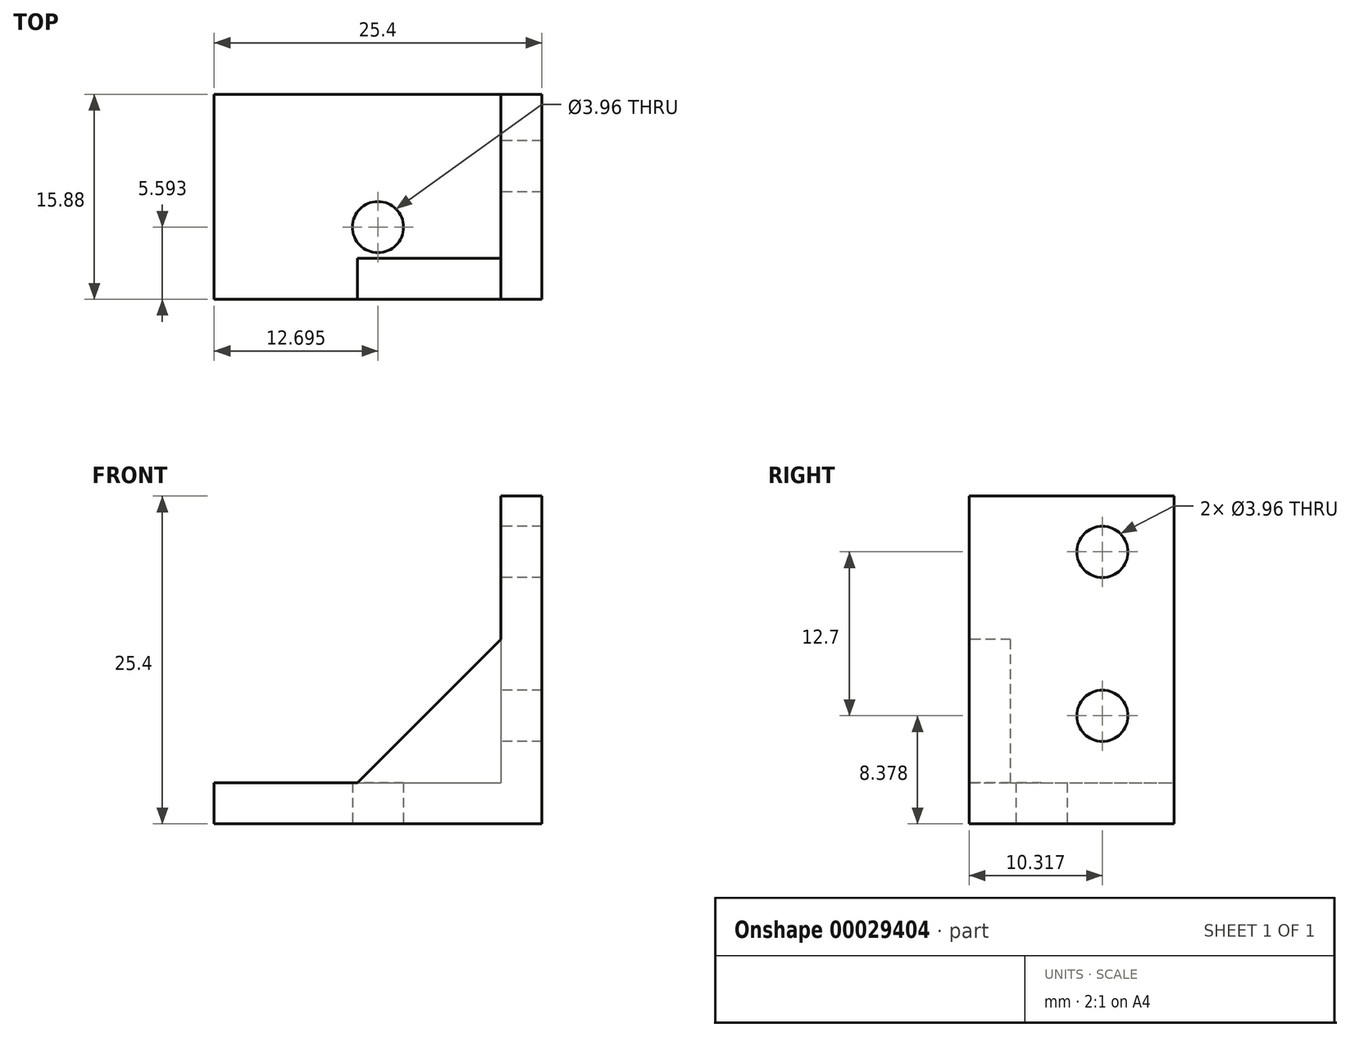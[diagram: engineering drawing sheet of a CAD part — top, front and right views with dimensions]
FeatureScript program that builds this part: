
annotation { "Feature Type Name" : "Feature", "Feature Type Description" : "" }
export const myFeature = defineFeature(function(context is Context, id is Id, definition is map)
    precondition{}
    {
        {
            var Q0;
            Q0=qCreatedBy(makeId("Front.planeOp"),FACE);
            var sketch = newSketch(context, id + "F0", { "sketchPlane" : qUnion([Q0])});
            skLineSegment(sketch, "E0.bottom", {"start": v(-17.16, -5.26) * mm, "end": v(5.06, -5.26) * mm});
            skLineSegment(sketch, "E0.top", {"start": v(-17.16, -8.43) * mm, "end": v(8.24, -8.43) * mm});
            skLineSegment(sketch, "E0.left", {"start": v(-17.16, -5.26) * mm, "end": v(-17.16, -8.43) * mm});
            skLineSegment(sketch, "E0.right", {"start": v(8.24, -5.26) * mm, "end": v(8.24, -8.43) * mm});
            skLineSegment(sketch, "E1", {"start": v(8.24, 16.97) * mm, "end": v(8.24, -8.43) * mm});
            skLineSegment(sketch, "E2", {"start": v(8.24, 16.97) * mm, "end": v(5.06, 16.97) * mm});
            skLineSegment(sketch, "E3", {"start": v(5.06, 16.97) * mm, "end": v(5.06, -5.26) * mm});
            skLineSegment(sketch, "E4", {"start": v(5.06, 5.85) * mm, "end": v(-6.05, -5.26) * mm});
            skLineSegment(sketch, "E5", {"start": v(-2.38, 7.14) * mm, "end": v(7.14, -2.38) * mm});
            skSolve(sketch);
        }
        {
            var Q0;
            {var subQ5=sQuery(id+"F0.wireOp",EDGE,"E0.top");Q0=makeQuery(id+"F0.imprint","IMPRINT",FACE,{"disambiguationData":[TD([[makeQuery(id+"F0.imprint","IMPRINT",EDGE,{"derivedFrom":subQ5}),1.0]])]});}
            extrude(context, id + "F1", {"entities" : qUnion([Q0]), "depth" : 15.88 * mm});
        }
        {
            var Q0;
            Q0=makeQuery(id+"F1.opExtrude","CAP_FACE",FACE,{"disambiguationData":[OSD([sQuery(id+"F0.wireOp",EDGE,"E0.bottom"),sQuery(id+"F0.wireOp",EDGE,"E0.top"),sQuery(id+"F0.wireOp",EDGE,"E0.left"),sQuery(id+"F0.wireOp",EDGE,"E1"),sQuery(id+"F0.wireOp",EDGE,"E2"),sQuery(id+"F0.wireOp",EDGE,"E3")])],"isStart":false});
            var sketch = newSketch(context, id + "F2", { "sketchPlane" : qUnion([Q0])});
            skLineSegment(sketch, "E6", {"start": v(5.06, 5.85) * mm, "end": v(-6.05, -5.26) * mm});
            skSolve(sketch);
        }
        {
            var Q0;
            {var subQ1=sQuery(id+"F2.wireOp",EDGE,"E6");Q0=makeQuery(id+"F2.imprint","IMPRINT",FACE,{"disambiguationData":[TD([[makeQuery(id+"F2.imprint","IMPRINT",EDGE,{"derivedFrom":subQ1}),1.0]])]});}
            extrude(context, id + "F3", {"entities" : qUnion([Q0]), "operationType" : NewBodyOperationType.ADD, "oppositeDirection" : true, "depth" : 3.17 * mm});
        }
        {
            var Q0;
            Q0=makeQuery(id+"F1.opExtrude","SWEPT_FACE",FACE,{"disambiguationData":[OSD([sQuery(id+"F0.wireOp",EDGE,"E3")])]});
            var sketch = newSketch(context, id + "F4", { "sketchPlane" : qUnion([Q0])});
            skCircle(sketch, "E7", {"center": v(5.56, 12.65) * mm, "radius": 1.98 * mm});
            skCircle(sketch, "E8", {"center": v(5.56, -0.05) * mm, "radius": 1.98 * mm});
            skSolve(sketch);
        }
        {
            var Q0;
            Q0=makeQuery(id+"F4.imprint","IMPRINT",FACE,{"disambiguationData":[TD([[makeQuery(id+"F4.imprint","IMPRINT",EDGE,{"derivedFrom":sQuery(id+"F4.wireOp",EDGE,"E7")}),1.0]])]});
            var Q1;
            Q1=makeQuery(id+"F4.imprint","IMPRINT",FACE,{"disambiguationData":[TD([[makeQuery(id+"F4.imprint","IMPRINT",EDGE,{"derivedFrom":sQuery(id+"F4.wireOp",EDGE,"E8")}),1.0]])]});
            extrude(context, id + "F5", {"entities" : qUnion([Q0, Q1]), "operationType" : NewBodyOperationType.REMOVE, "oppositeDirection" : true, "depth" : 25.4 * mm});
        }
        {
            var Q0;
            Q0=makeQuery(id+"F1.opExtrude","SWEPT_FACE",FACE,{"disambiguationData":[OSD([sQuery(id+"F0.wireOp",EDGE,"E0.top")])]});
            var sketch = newSketch(context, id + "F6", { "sketchPlane" : qUnion([Q0])});
            skCircle(sketch, "E9", {"center": v(-4.46, 10.29) * mm, "radius": 1.98 * mm});
            skSolve(sketch);
        }
        {
            var Q0;
            Q0=makeQuery(id+"F6.imprint","IMPRINT",FACE,{"disambiguationData":[TD([[makeQuery(id+"F6.imprint","IMPRINT",EDGE,{"derivedFrom":sQuery(id+"F6.wireOp",EDGE,"E9")}),1.0]])]});
            extrude(context, id + "F7", {"entities" : qUnion([Q0]), "operationType" : NewBodyOperationType.REMOVE, "oppositeDirection" : true, "depth" : 25.4 * mm});
        }
    });
